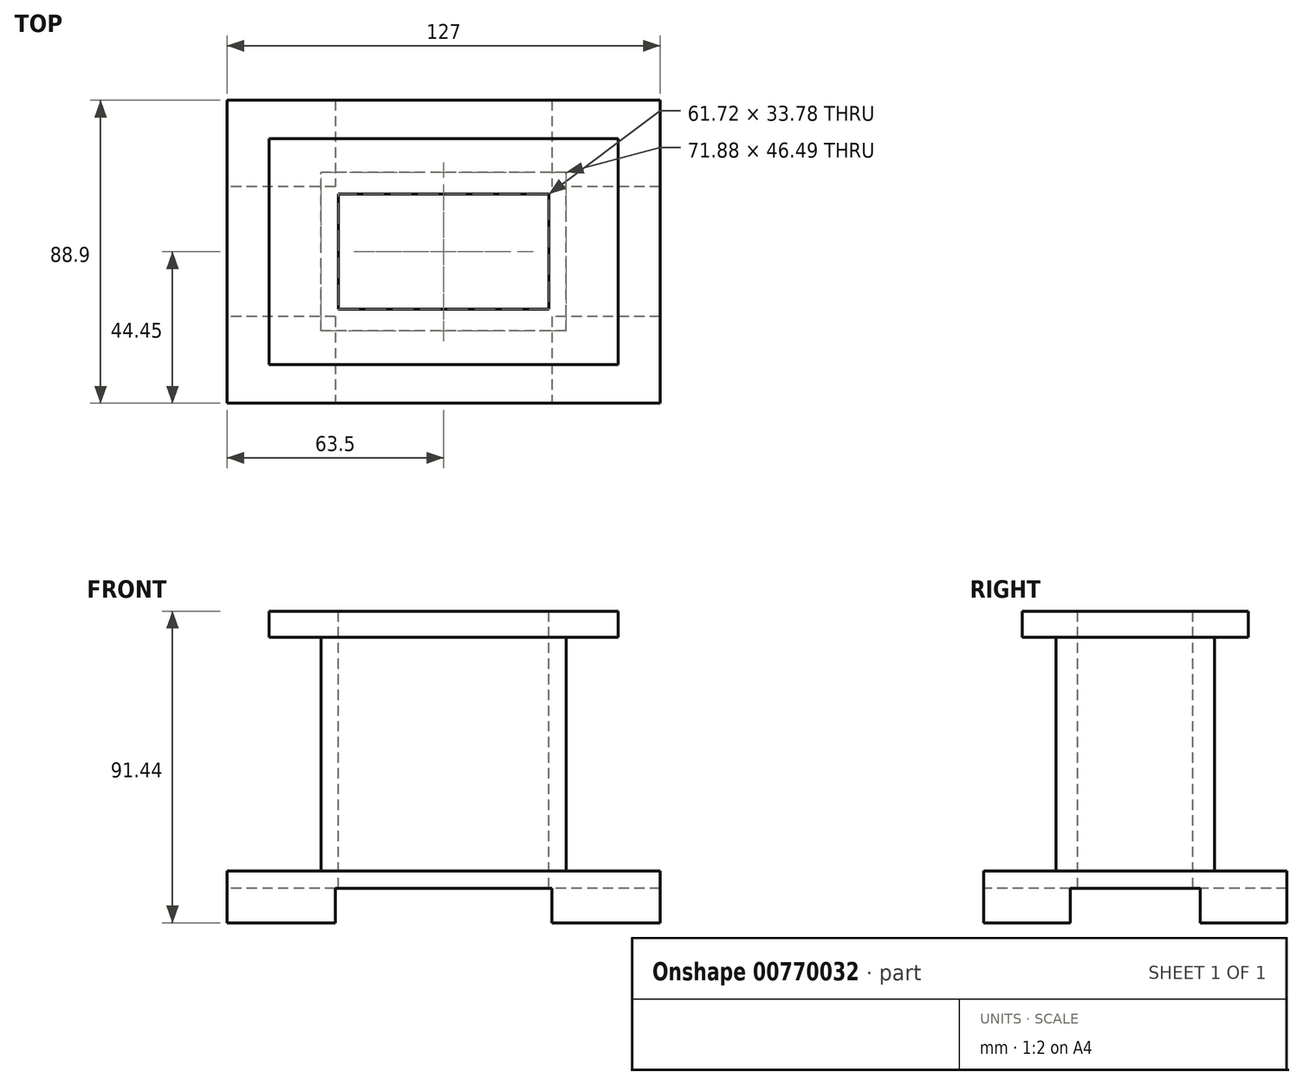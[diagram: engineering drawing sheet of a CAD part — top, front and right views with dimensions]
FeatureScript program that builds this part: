
annotation { "Feature Type Name" : "Feature", "Feature Type Description" : "" }
export const myFeature = defineFeature(function(context is Context, id is Id, definition is map)
    precondition{}
    {
        {
            var Q0;
            Q0=qCreatedBy(makeId("Top.planeOp"),FACE);
            var sketch = newSketch(context, id + "F0", { "sketchPlane" : qUnion([Q0])});
            skLineSegment(sketch, "E0.bottom", {"start": v(63.5, 44.45) * mm, "end": v(-63.5, 44.45) * mm});
            skLineSegment(sketch, "E0.top", {"start": v(63.5, -44.45) * mm, "end": v(-63.5, -44.45) * mm});
            skLineSegment(sketch, "E0.left", {"start": v(63.5, 44.45) * mm, "end": v(63.5, -44.45) * mm});
            skLineSegment(sketch, "E0.right", {"start": v(-63.5, 44.45) * mm, "end": v(-63.5, -44.45) * mm});
            skPoint(sketch, "E0.middle", {"position": v(0, 0) * mm});
            skSolve(sketch);
        }
        {
            var Q0;
            Q0=makeQuery(id+"F0.imprint","IMPRINT",FACE,{"disambiguationData":[TD([[makeQuery(id+"F0.imprint","IMPRINT",EDGE,{"derivedFrom":sQuery(id+"F0.wireOp",EDGE,"E0.bottom")}),1.0]])]});
            extrude(context, id + "F1", {"entities" : qUnion([Q0]), "oppositeDirection" : true, "depth" : 15.24 * mm, "offsetDistance" : 25.4 * mm});
        }
        {
            var Q0;
            Q0=makeQuery(id+"F1.opExtrude","SWEPT_FACE",FACE,{"disambiguationData":[OSD([sQuery(id+"F0.wireOp",EDGE,"E0.top")])]});
            var sketch = newSketch(context, id + "F2", { "sketchPlane" : qUnion([Q0])});
            skLineSegment(sketch, "E1.bottom", {"start": v(-31.75, -15.24) * mm, "end": v(31.75, -15.24) * mm});
            skLineSegment(sketch, "E1.top", {"start": v(-31.75, -5.08) * mm, "end": v(31.75, -5.08) * mm});
            skLineSegment(sketch, "E1.left", {"start": v(-31.75, -15.24) * mm, "end": v(-31.75, -5.08) * mm});
            skLineSegment(sketch, "E1.right", {"start": v(31.75, -15.24) * mm, "end": v(31.75, -5.08) * mm});
            skSolve(sketch);
        }
        {
            var Q0;
            Q0=makeQuery(id+"F2.imprint","IMPRINT",FACE,{"disambiguationData":[TD([[makeQuery(id+"F2.imprint","IMPRINT",EDGE,{"derivedFrom":sQuery(id+"F2.wireOp",EDGE,"E1.bottom")}),-1.0]])]});
            extrude(context, id + "F3", {"entities" : qUnion([Q0]), "operationType" : NewBodyOperationType.REMOVE, "oppositeDirection" : true, "depth" : 88.9 * mm, "offsetDistance" : 25.4 * mm});
        }
        {
            var Q0;
            Q0=makeQuery(id+"F1.opExtrude","SWEPT_FACE",FACE,{"disambiguationData":[OSD([sQuery(id+"F0.wireOp",EDGE,"E0.right")])]});
            var sketch = newSketch(context, id + "F4", { "sketchPlane" : qUnion([Q0])});
            skLineSegment(sketch, "E2.bottom", {"start": v(-19.05, -15.24) * mm, "end": v(19.05, -15.24) * mm});
            skLineSegment(sketch, "E2.top", {"start": v(-19.05, -5.08) * mm, "end": v(19.05, -5.08) * mm});
            skLineSegment(sketch, "E2.left", {"start": v(-19.05, -15.24) * mm, "end": v(-19.05, -5.08) * mm});
            skLineSegment(sketch, "E2.right", {"start": v(19.05, -15.24) * mm, "end": v(19.05, -5.08) * mm});
            skSolve(sketch);
        }
        {
            var Q0;
            Q0=makeQuery(id+"F4.imprint","IMPRINT",FACE,{"disambiguationData":[TD([[makeQuery(id+"F4.imprint","IMPRINT",EDGE,{"derivedFrom":sQuery(id+"F4.wireOp",EDGE,"E2.bottom")}),1.0]])]});
            extrude(context, id + "F5", {"entities" : qUnion([Q0]), "operationType" : NewBodyOperationType.REMOVE, "oppositeDirection" : true, "depth" : 127 * mm, "offsetDistance" : 25.4 * mm});
        }
        {
            var Q0;
            Q0=makeQuery(id+"F1.opExtrude","CAP_FACE",FACE,{"disambiguationData":[OSD([sQuery(id+"F0.wireOp",EDGE,"E0.bottom"),sQuery(id+"F0.wireOp",EDGE,"E0.top"),sQuery(id+"F0.wireOp",EDGE,"E0.left"),sQuery(id+"F0.wireOp",EDGE,"E0.right")])],"isStart":true});
            var sketch = newSketch(context, id + "F6", { "sketchPlane" : qUnion([Q0])});
            skLineSegment(sketch, "E3.bottom", {"start": v(35.94, -23.24) * mm, "end": v(-35.94, -23.24) * mm});
            skLineSegment(sketch, "E3.top", {"start": v(35.94, 23.24) * mm, "end": v(-35.94, 23.24) * mm});
            skLineSegment(sketch, "E3.left", {"start": v(35.94, -23.24) * mm, "end": v(35.94, 23.24) * mm});
            skLineSegment(sketch, "E3.right", {"start": v(-35.94, -23.24) * mm, "end": v(-35.94, 23.24) * mm});
            skPoint(sketch, "E3.middle", {"position": v(0, 0) * mm});
            skSolve(sketch);
        }
        {
            var Q0;
            Q0=makeQuery(id+"F6.imprint","IMPRINT",FACE,{"disambiguationData":[TD([[makeQuery(id+"F6.imprint","IMPRINT",EDGE,{"derivedFrom":sQuery(id+"F6.wireOp",EDGE,"E3.bottom")}),-1.0]])]});
            extrude(context, id + "F7", {"entities" : qUnion([Q0]), "operationType" : NewBodyOperationType.ADD, "depth" : 76.2 * mm, "offsetDistance" : 25.4 * mm});
        }
        {
            var Q0;
            Q0=makeQuery(id+"F7.opExtrude","CAP_FACE",FACE,{"disambiguationData":[OSD([sQuery(id+"F6.wireOp",EDGE,"E3.bottom"),sQuery(id+"F6.wireOp",EDGE,"E3.top"),sQuery(id+"F6.wireOp",EDGE,"E3.left"),sQuery(id+"F6.wireOp",EDGE,"E3.right")])],"isStart":false});
            var sketch = newSketch(context, id + "F8", { "sketchPlane" : qUnion([Q0])});
            skLineSegment(sketch, "E4.bottom", {"start": v(30.86, 16.89) * mm, "end": v(-30.86, 16.89) * mm});
            skLineSegment(sketch, "E4.top", {"start": v(30.86, -16.89) * mm, "end": v(-30.86, -16.89) * mm});
            skLineSegment(sketch, "E4.left", {"start": v(30.86, 16.89) * mm, "end": v(30.86, -16.89) * mm});
            skLineSegment(sketch, "E4.right", {"start": v(-30.86, 16.89) * mm, "end": v(-30.86, -16.89) * mm});
            skPoint(sketch, "E4.middle", {"position": v(0, 0) * mm});
            skSolve(sketch);
        }
        {
            var Q0;
            Q0=makeQuery(id+"F8.imprint","IMPRINT",FACE,{"disambiguationData":[TD([[makeQuery(id+"F8.imprint","IMPRINT",EDGE,{"derivedFrom":sQuery(id+"F8.wireOp",EDGE,"E4.bottom")}),1.0]])]});
            extrude(context, id + "F9", {"entities" : qUnion([Q0]), "operationType" : NewBodyOperationType.REMOVE, "oppositeDirection" : true, "depth" : 101.6 * mm, "offsetDistance" : 25.4 * mm});
        }
        {
            var Q0;
            Q0=makeQuery(id+"F7.opExtrude","CAP_FACE",FACE,{"disambiguationData":[OSD([sQuery(id+"F6.wireOp",EDGE,"E3.bottom"),sQuery(id+"F6.wireOp",EDGE,"E3.top"),sQuery(id+"F6.wireOp",EDGE,"E3.left"),sQuery(id+"F6.wireOp",EDGE,"E3.right")])],"isStart":false});
            var sketch = newSketch(context, id + "F10", { "sketchPlane" : qUnion([Q0])});
            skLineSegment(sketch, "E5.bottom", {"start": v(51.18, 33.14) * mm, "end": v(-51.18, 33.14) * mm});
            skLineSegment(sketch, "E5.top", {"start": v(51.18, -33.14) * mm, "end": v(-51.18, -33.14) * mm});
            skLineSegment(sketch, "E5.left", {"start": v(51.18, 33.14) * mm, "end": v(51.18, -33.14) * mm});
            skLineSegment(sketch, "E5.right", {"start": v(-51.18, 33.14) * mm, "end": v(-51.18, -33.14) * mm});
            skPoint(sketch, "E5.middle", {"position": v(0, 0) * mm});
            skSolve(sketch);
        }
        {
            var Q0;
            Q0=makeQuery(id+"F10.imprint","IMPRINT",FACE,{"disambiguationData":[TD([[makeQuery(id+"F10.imprint","IMPRINT",EDGE,{"derivedFrom":sQuery(id+"F10.wireOp",EDGE,"E5.bottom")}),1.0]])]});
            extrude(context, id + "F11", {"entities" : qUnion([Q0]), "operationType" : NewBodyOperationType.ADD, "oppositeDirection" : true, "depth" : 7.62 * mm, "offsetDistance" : 25.4 * mm});
        }
    });
